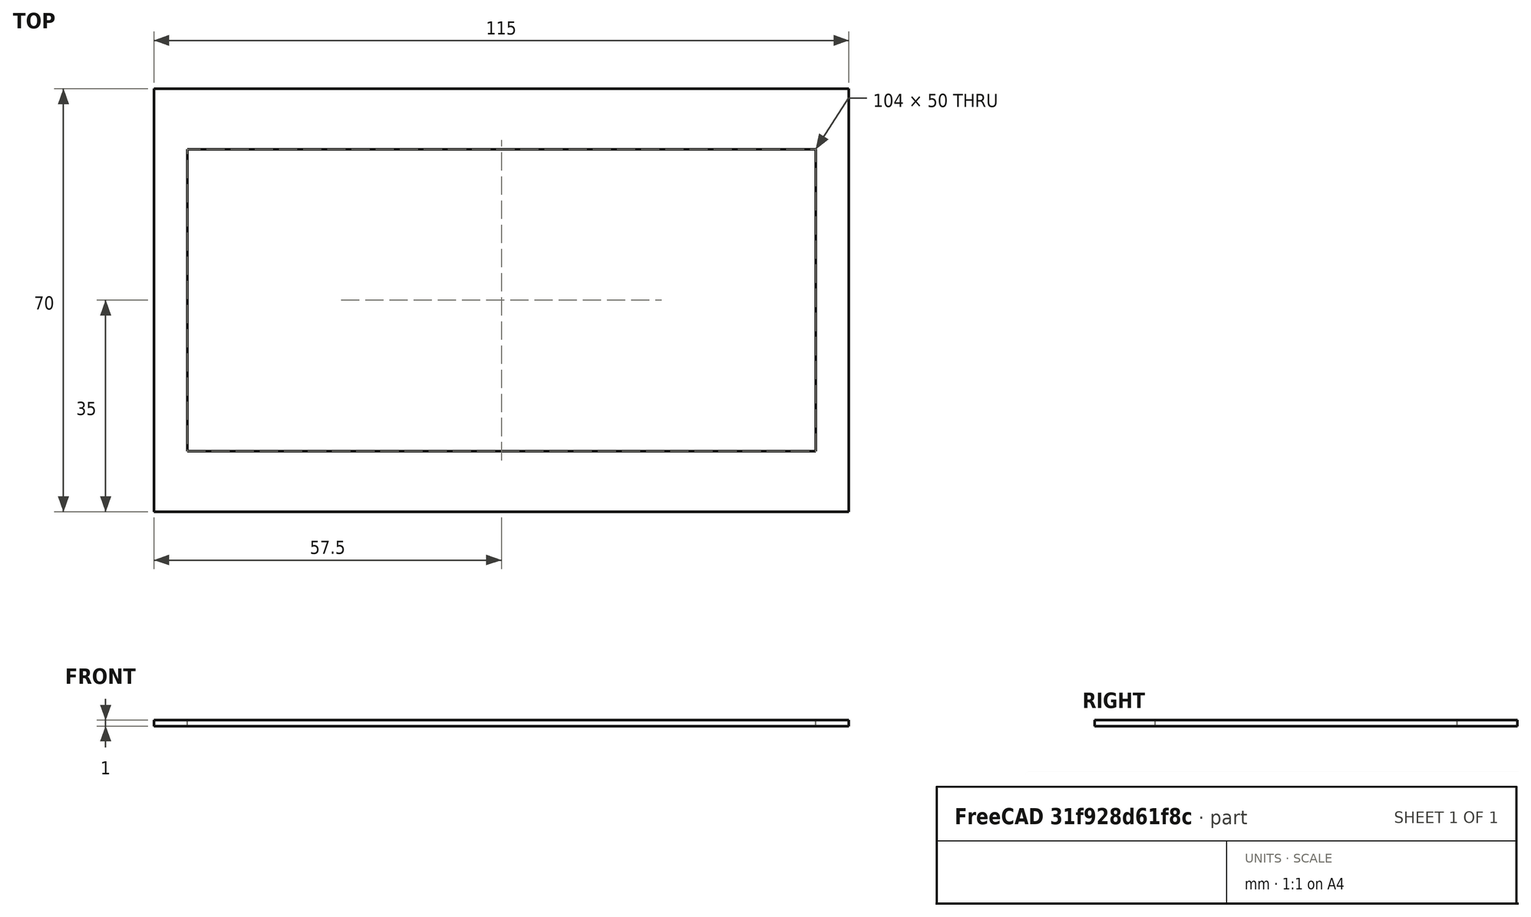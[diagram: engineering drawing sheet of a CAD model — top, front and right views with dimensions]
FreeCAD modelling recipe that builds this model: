
FCSTD DOCUMENT  (FreeCAD 0.20R26720 (Git))
Label: coin_insert_frame
License: All rights reserved
LicenseURL: http://en.wikipedia.org/wiki/All_rights_reserved
objects: Sketcher::SketchObject×1, PartDesign::Pad×1, PartDesign::Body×1
note: 4 computed .brp shape members not serialized (recipe doc carries the construction recipe); baked Part::Feature solids carry a one-line shape summary decoded from their .brp

FEATURE [Sketcher::SketchObject] Sketch
  FullyConstrained = true
  MapMode = 5
  Support = -> [XY_Plane]
  sketch-geometry (8):
    g0: LineSegment StartX=-57.5 StartY=35 StartZ=0 EndX=57.5 EndY=35 EndZ=0
    g1: LineSegment StartX=57.5 StartY=35 StartZ=0 EndX=57.5 EndY=-35 EndZ=0
    g2: LineSegment StartX=57.5 StartY=-35 StartZ=0 EndX=-57.5 EndY=-35 EndZ=0
    g3: LineSegment StartX=-57.5 StartY=-35 StartZ=0 EndX=-57.5 EndY=35 EndZ=0
    g4: LineSegment StartX=-52 StartY=25 StartZ=0 EndX=52 EndY=25 EndZ=0
    g5: LineSegment StartX=52 StartY=25 StartZ=0 EndX=52 EndY=-25 EndZ=0
    g6: LineSegment StartX=52 StartY=-25 StartZ=0 EndX=-52 EndY=-25 EndZ=0
    g7: LineSegment StartX=-52 StartY=-25 StartZ=0 EndX=-52 EndY=25 EndZ=0
  constraints (20):
    c: Coincident(g0,g1)
    c: Coincident(g1,g2)
    c: Coincident(g2,g3)
    c: Coincident(g3,g0)
    c: Horizontal(g2)
    c: Vertical(g1)
    c: Distance(g3) = 70
    c: Distance(g0) = 115
    c: Symmetric(g0,g0,g-2)
    c: Symmetric(g0,g2,g-1)
    c: Coincident(g4,g5)
    c: Coincident(g5,g6)
    c: Coincident(g6,g7)
    c: Coincident(g7,g4)
    c: Horizontal(g6)
    c: Vertical(g5)
    c: Distance(g4) = 104
    c: Distance(g7) = 50
    c: Symmetric(g4,g6,g-1)
    c: Symmetric(g4,g4,g-2)
FEATURE [PartDesign::Pad] Pad
  Direction = (0,0,1)
  Length = 1
  Length2 = 100
  Profile = -> Sketch
  ReferenceAxis = -> Sketch [N_Axis]
  Type = 0
FEATURE [PartDesign::Body] Body
  Group = -> [Sketch,Pad]
  Origin = -> Origin
  Tip = -> Pad
